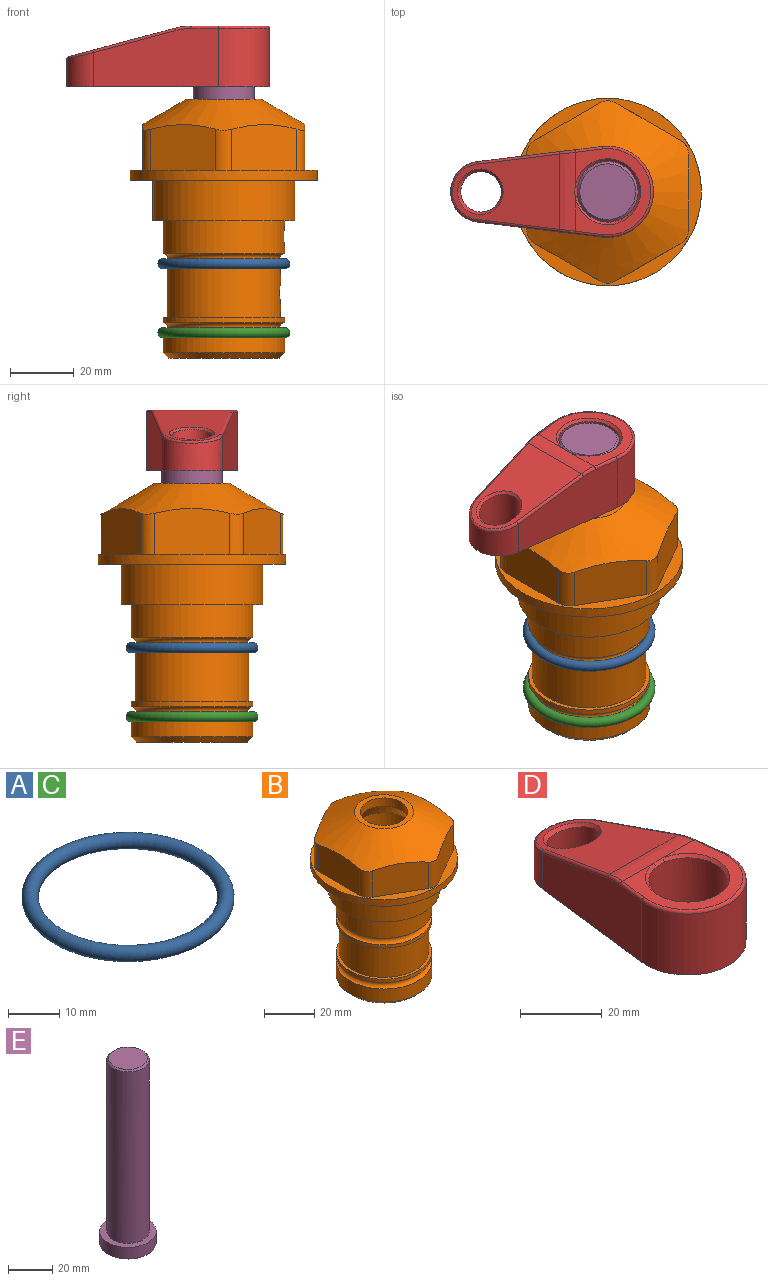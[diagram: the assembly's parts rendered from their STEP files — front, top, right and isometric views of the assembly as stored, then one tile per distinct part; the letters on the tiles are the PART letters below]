
ASSEMBLY  parts=5 mates=4
PART A: 1 faces, bbox 44.7x44.7x3.2 mm
  f0: torus R=19.05mm, axis (0,0,1), area 1193.9mm2
PART B: 36 faces, bbox 58.7x58.7x81 mm
  f0: cylinder r=17.78mm len=35.56mm, axis (0,0,1), area 1670.8mm2, adj f23,f24,f31
  f1: cylinder r=19.05mm len=38.1mm, axis (0,0,1), area 1191.9mm2, adj f26,f27,f30
  f2: plane 58.66x58.66mm, normal (0,0,-1), area 1150.6mm2, adj f3,f28
  f3: cylinder r=29.33mm len=58.66mm, axis (0,0,-1), area 585.1mm2, adj f2,f4
  f4: plane 58.66x58.66mm, normal (0,0,1), area 475.9mm2, adj f3,f5,f6,f7,f8,f9,f10,f11
  f5: plane 20.32x14.34mm, normal (-0.5,0.87,0), area 324.4mm2, adj f4,f15,f16,f17
  f6: plane 20.32x14.34mm, normal (0.5,0.87,0), area 324.4mm2, adj f4,f14,f15,f17
  f7: plane 23.48x14.34mm, normal (1,0,0), area 324.4mm2, adj f4,f13,f14,f17
  f8: plane 20.32x14.34mm, normal (0.5,-0.87,0), area 324.4mm2, adj f4,f12,f13,f17
  f9: plane 20.32x14.34mm, normal (-0.5,-0.87,0), area 324.4mm2, adj f4,f11,f12,f17
  f10: plane 23.48x14.34mm, normal (-1,0,0), area 324.4mm2, adj f4,f11,f16,f17
  f11: cylinder r=5.08mm len=12.85mm, axis (0,0,-1), area 67.2mm2, adj f4,f9,f10,f17
  f12: cylinder r=5.08mm len=12.85mm, axis (0,0,-1), area 67.2mm2, adj f4,f8,f9,f17
  f13: cylinder r=5.08mm len=12.85mm, axis (0,0,-1), area 67.2mm2, adj f4,f7,f8,f17
  f14: cylinder r=5.08mm len=12.85mm, axis (0,0,-1), area 67.2mm2, adj f4,f6,f7,f17
  f15: cylinder r=5.08mm len=12.85mm, axis (0,0,-1), area 67.2mm2, adj f4,f5,f6,f17
  f16: cylinder r=5.08mm len=12.85mm, axis (0,0,-1), area 67.2mm2, adj f4,f5,f10,f17
  f17: cone r=11.73mm half-angle=60deg, axis (0,0,-1), area 2071.8mm2, adj f5,f6,f7,f8,f9,f10,f11,f12
  f18: plane 23.46x23.46mm, normal (0,0,1), area 147.4mm2, adj f17,f35
  f19: plane 34.93x34.93mm, normal (0,0,-1), area 958mm2, adj f29
  f20: cylinder r=19.05mm len=38.1mm, axis (0,0,1), area 760.1mm2, adj f21,f29
  f21: torus R=19.05mm, axis (0,0,1), area 565.3mm2, adj f20,f22
  f22: cylinder r=19.05mm len=38.1mm, axis (0,0,1), area 190mm2, adj f21,f23
  f23: plane 38.1x38.1mm, normal (0,0,1), area 146.9mm2, adj f0,f22
  f24: plane 38.1x38.1mm, normal (0,0,-1), area 146.9mm2, adj f0,f25
  f25: cylinder r=19.05mm len=38.1mm, axis (0,0,1), area 190mm2, adj f24,f26
  f26: torus R=19.05mm, axis (0,0,1), area 565.3mm2, adj f1,f25
  f27: plane 44.45x44.45mm, normal (0,0,-1), area 411.7mm2, adj f1,f28
  f28: cylinder r=22.23mm len=44.45mm, axis (0,0,1), area 1773.5mm2, adj f2,f27
  f29: cone r=19.05mm half-angle=45deg, axis (0,0,1), area 257.5mm2, adj f19,f20
  f30: cylinder r=3.17mm len=6.75mm, axis (-1,0,0), area 128mm2, adj f1,f33
  f31: cylinder r=3.17mm len=6.35mm, axis (-1,0,0), area 102.5mm2, adj f0,f33
  f32: plane 25.4x25.4mm, normal (0,0,1), area 506.7mm2, adj f33
  f33: cylinder r=12.7mm len=66.42mm, axis (0,0,-1), area 5236.2mm2, adj f30,f31,f32,f34
  f34: cone r=9.53mm half-angle=30deg, axis (0,0,-1), area 443.4mm2, adj f33,f35
  f35: cylinder r=9.53mm len=19.05mm, axis (0,0,-1), area 240.9mm2, adj f18,f34
PART C: same geometry as A
PART D: 31 faces, bbox 31.7x65.5x19.8 mm
  f0: plane 39.12x18.26mm, normal (0.99,0.12,0), area 612.2mm2, adj f1,f4,f7,f11,f13,f15
  f1: cylinder r=9.53mm len=18.91mm, axis (0,0,-1), area 296.1mm2, adj f0,f2,f7,f17
  f2: plane 39.12x18.26mm, normal (-0.99,0.12,0), area 612.2mm2, adj f1,f4,f7,f12,f14,f16
  f3: cylinder r=6.35mm len=12.7mm, axis (0,0,-1), area 362.4mm2, adj f7,f18
  f4: cylinder r=14.29mm len=28.58mm, axis (0,0,-1), area 882.2mm2, adj f0,f2,f7,f10
  f5: cylinder r=9.53mm len=19.05mm, axis (0,0,-1), area 1092.6mm2, adj f7,f19,f20
  f6: plane 26.99x23.69mm, normal (0,0,1), area 216.2mm2, adj f9,f10,f11,f12,f19
  f7: plane 63.5x28.58mm, normal (0,0,-1), area 661.8mm2, adj f0,f1,f2,f3,f4,f5,f22,f23
  f8: plane 33.52x23.6mm, normal (0,0.26,0.97), area 486mm2, adj f9,f15,f16,f17,f18
  f9: cylinder r=19.05mm len=24.72mm, axis (1,0,0), area 120.4mm2, adj f6,f8,f13,f14,f20
  f10: torus R=13.49mm, axis (0,0,1), area 59mm2, adj f4,f6,f11,f12
  f11: cylinder r=0.79mm len=8.67mm, axis (0.12,-0.99,0), area 10.8mm2, adj f0,f6,f10,f13
  f12: cylinder r=0.79mm len=8.67mm, axis (0.12,0.99,0), area 10.8mm2, adj f2,f6,f10,f14
  f13: bspline ~4.95x1.42mm, area 6.1mm2, adj f0,f9,f11,f15
  f14: bspline ~4.95x1.42mm, area 6.1mm2, adj f2,f9,f12,f16
  f15: cylinder r=0.79mm len=25.95mm, axis (0.12,-0.96,0.26), area 32.9mm2, adj f0,f8,f13,f17
  f16: cylinder r=0.79mm len=25.95mm, axis (0.12,0.96,-0.26), area 32.9mm2, adj f2,f8,f14,f17
  f17: bspline ~18.91x8.38mm, area 30mm2, adj f1,f8,f15,f16
  f18: bspline ~14.29x14.29mm, area 48.3mm2, adj f3,f8
  f19: cone r=9.53mm half-angle=45deg, axis (0,0,1), area 66.5mm2, adj f5,f6,f20
  f20: bspline ~3.22x0.96mm, area 3.5mm2, adj f5,f9,f19
  f21: plane 2.75x2.72mm, normal (0,0,-1), area 2.9mm2, adj f23,f25,f28
  f22: plane 23.05x15.88mm, normal (-0.99,-0.12,0), area 323.6mm2, adj f7,f25,f26,f27,f28,f29
  f23: plane 23.05x15.88mm, normal (0.99,-0.12,0), area 323.6mm2, adj f7,f21,f25,f27,f28,f30
  f24: cylinder r=9.53mm len=10.69mm, axis (0,0,-1), area 114.7mm2, adj f7,f27,f29,f30
  f25: cylinder r=12.7mm len=20.59mm, axis (0,0,-1), area 381.1mm2, adj f7,f21,f22,f23,f26,f28
  f26: plane 2.75x2.72mm, normal (0,0,-1), area 2.9mm2, adj f22,f25,f28
  f27: plane 19.72x18.37mm, normal (0,-0.26,-0.97), area 291.8mm2, adj f22,f23,f24,f28,f29,f30
  f28: cylinder r=15.88mm len=19.92mm, axis (1,0,0), area 54.8mm2, adj f21,f22,f23,f25,f26,f27
  f29: cylinder r=1.59mm len=11mm, axis (0,0,-1), area 34.7mm2, adj f7,f22,f24,f27
  f30: cylinder r=1.59mm len=11mm, axis (0,0,-1), area 34.7mm2, adj f7,f23,f24,f27
PART E: 6 faces, bbox 25.4x25.4x101.6 mm
  f0: plane 17.46x17.46mm, normal (0,0,1), area 239.5mm2, adj f5
  f1: plane 25.4x25.4mm, normal (0,0,-1), area 506.7mm2, adj f2
  f2: cylinder r=12.7mm len=25.4mm, axis (0,0,1), area 506.7mm2, adj f1,f3
  f3: plane 25.4x25.4mm, normal (0,0,1), area 221.7mm2, adj f2,f4
  f4: cylinder r=9.53mm len=94.46mm, axis (0,0,1), area 5653mm2, adj f3,f5
  f5: cone r=8.73mm half-angle=45deg, axis (0,0,-1), area 64.4mm2, adj f0,f4
PLACE A t=(0,0,-1.59)mm
PLACE B at identity fixed
PLACE C t=(0,0,-23.18)mm
PLACE D rot(axis=(0,0,1),90deg) t=(0,0,-15.14)mm
PLACE E rot(axis=(0,0,1),90deg) t=(0,0,-15.94)mm
MATE cylindrical E.f2 <-> B.f0  axis (0,0,-1) through (0,0,-54.04)mm
MATE fastened C.f0 <-> B.f0  axis (0,0,1) through (0,0,-47.69)mm
MATE fastened A.f0 <-> B.f0  axis (0,0,1) through (0,0,-26.1)mm
MATE fastened E.f2 <-> D.f4  axis (0,0,1) through (0,0,47.56)mm
